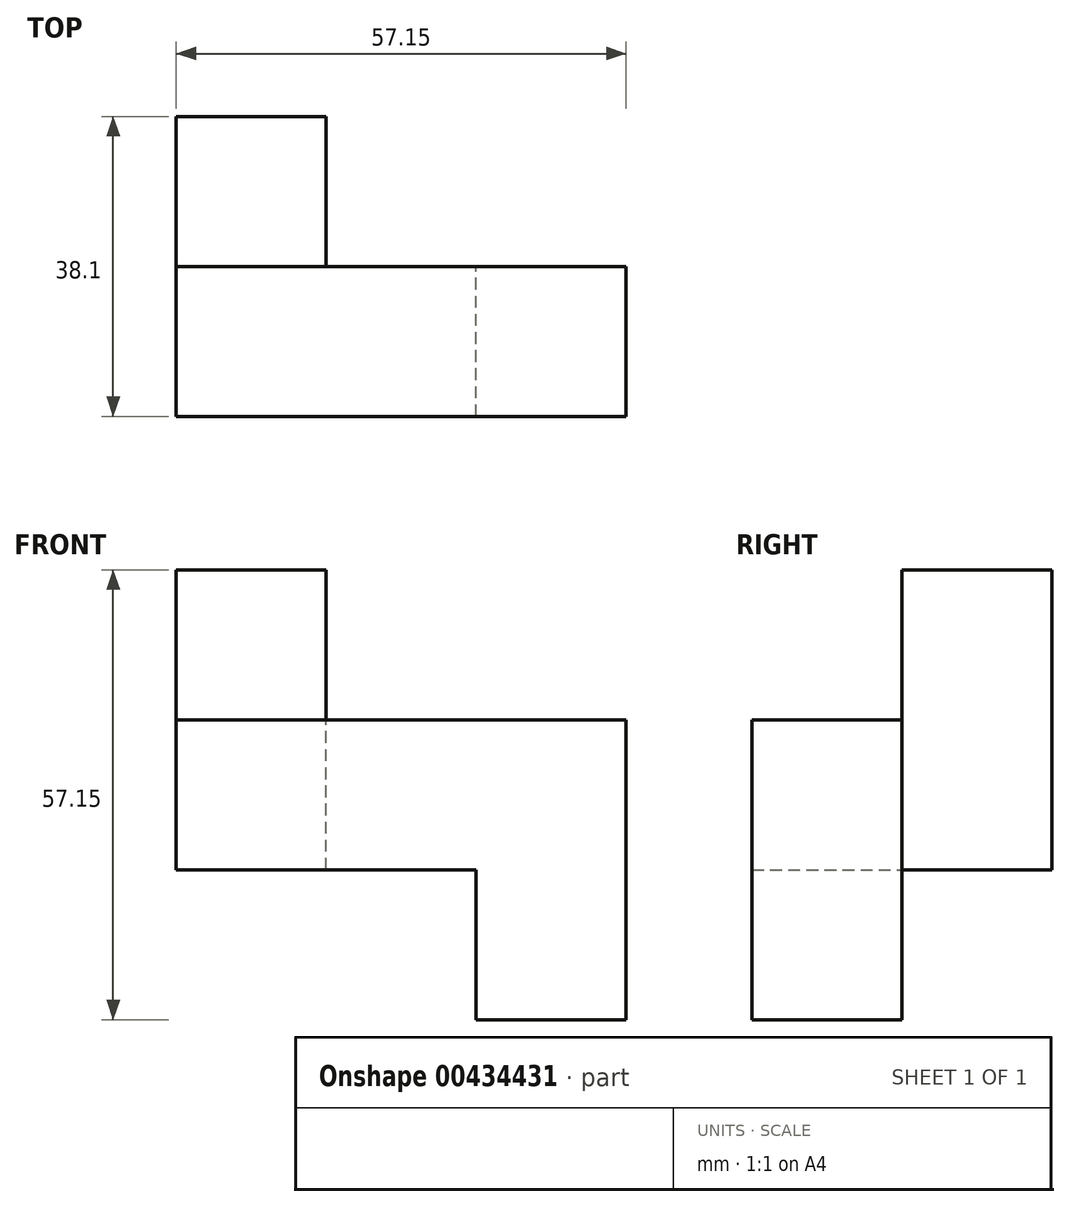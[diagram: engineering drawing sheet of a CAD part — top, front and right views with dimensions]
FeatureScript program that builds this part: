
annotation { "Feature Type Name" : "Feature", "Feature Type Description" : "" }
export const myFeature = defineFeature(function(context is Context, id is Id, definition is map)
    precondition{}
    {
        {
            var Q0;
            Q0=qCreatedBy(makeId("Front.planeOp"),FACE);
            var sketch = newSketch(context, id + "F0", { "sketchPlane" : qUnion([Q0])});
            skLineSegment(sketch, "E0", {"start": v(-62.24, 53.61) * mm, "end": v(-62.24, -50.56) * mm});
            skLineSegment(sketch, "E1", {"start": v(-62.24, -50.56) * mm, "end": v(31.63, -50.56) * mm});
            skLineSegment(sketch, "E2", {"start": v(31.63, -50.56) * mm, "end": v(31.63, 53.61) * mm});
            skLineSegment(sketch, "E3", {"start": v(31.63, 53.61) * mm, "end": v(-62.24, 53.61) * mm});
            skLineSegment(sketch, "E4", {"start": v(-43.91, 19.05) * mm, "end": v(-43.91, -38.1) * mm});
            skLineSegment(sketch, "E5", {"start": v(-43.91, 19.05) * mm, "end": v(-24.86, 19.05) * mm});
            skLineSegment(sketch, "E6", {"start": v(-24.86, 19.05) * mm, "end": v(-24.86, 0) * mm});
            skLineSegment(sketch, "E7", {"start": v(-24.86, 0) * mm, "end": v(13.24, 0) * mm});
            skLineSegment(sketch, "E8", {"start": v(13.24, 0) * mm, "end": v(13.24, -38.1) * mm});
            skLineSegment(sketch, "E9", {"start": v(13.24, -38.1) * mm, "end": v(-43.91, -38.1) * mm});
            skLineSegment(sketch, "E10", {"start": v(-43.91, -38.1) * mm, "end": v(-24.86, -38.1) * mm});
            skPoint(sketch, "E11.endSnap0", {"position": v(13.24, -19.05) * mm});
            skLineSegment(sketch, "E12", {"start": v(-24.86, -19.05) * mm, "end": v(-43.91, -19.05) * mm});
            skLineSegment(sketch, "E13", {"start": v(-43.91, -19.05) * mm, "end": v(-5.81, -19.05) * mm});
            skPoint(sketch, "E13.endSnap0", {"position": v(-5.81, 0) * mm});
            skLineSegment(sketch, "E14", {"start": v(-5.81, -19.05) * mm, "end": v(-5.81, -38.1) * mm});
            skLineSegment(sketch, "E15", {"start": v(-5.81, -19.05) * mm, "end": v(13.24, -19.05) * mm});
            skLineSegment(sketch, "E16", {"start": v(-24.86, 0) * mm, "end": v(-43.91, 0) * mm});
            skLineSegment(sketch, "E17", {"start": v(-24.86, -19.05) * mm, "end": v(-24.86, 0) * mm});
            skSolve(sketch);
        }
        {
            var Q0;
            {var subQ4=sQuery(id+"F0.wireOp",EDGE,"E14");Q0=makeQuery(id+"F0.imprint","IMPRINT",FACE,{"disambiguationData":[TD([[makeQuery(id+"F0.imprint","IMPRINT",EDGE,{"derivedFrom":subQ4}),1.0]])]});}
            extrude(context, id + "F1", {"entities" : qUnion([Q0]), "depth" : 38.1 * mm});
        }
        {
            var Q0;
            {var subQ0=sQuery(id+"F0.wireOp",EDGE,"E7");Q0=makeQuery(id+"F0.imprint","IMPRINT",FACE,{"disambiguationData":[TD([[makeQuery(id+"F0.imprint","IMPRINT",EDGE,{"derivedFrom":subQ0}),-1.0]])]});}
            extrude(context, id + "F2", {"entities" : qUnion([Q0]), "operationType" : NewBodyOperationType.ADD, "depth" : 19.05 * mm});
        }
        {
            var Q0;
            {var subQ3=sQuery(id+"F0.wireOp",EDGE,"E16");Q0=makeQuery(id+"F0.imprint","IMPRINT",FACE,{"disambiguationData":[TD([[makeQuery(id+"F0.imprint","IMPRINT",EDGE,{"derivedFrom":subQ3}),1.0]])]});}
            extrude(context, id + "F3", {"entities" : qUnion([Q0]), "operationType" : NewBodyOperationType.ADD, "depth" : 19.05 * mm});
        }
        {
            var Q0;
            {var subQ3=sQuery(id+"F0.wireOp",EDGE,"E16");Q0=makeQuery(id+"F0.imprint","IMPRINT",FACE,{"disambiguationData":[TD([[makeQuery(id+"F0.imprint","IMPRINT",EDGE,{"derivedFrom":subQ3}),1.0]])]});}
            extrude(context, id + "F4", {"entities" : qUnion([Q0]), "operationType" : NewBodyOperationType.ADD, "oppositeDirection" : true, "depth" : 19.05 * mm});
        }
        {
            var Q0;
            {var subQ0=sQuery(id+"F0.wireOp",EDGE,"E5");Q0=makeQuery(id+"F0.imprint","IMPRINT",FACE,{"disambiguationData":[TD([[makeQuery(id+"F0.imprint","IMPRINT",EDGE,{"derivedFrom":subQ0}),-1.0]])]});}
            extrude(context, id + "F5", {"entities" : qUnion([Q0]), "operationType" : NewBodyOperationType.ADD, "oppositeDirection" : true, "depth" : 19.05 * mm});
        }
        {
            var Q0;
            Q0=makeQuery(id+"F1.opExtrude","SWEPT_FACE",FACE,{"disambiguationData":[OSD([sQuery(id+"F0.wireOp",EDGE,"E14")])]});
            var sketch = newSketch(context, id + "F6", { "sketchPlane" : qUnion([Q0])});
            skLineSegment(sketch, "E18", {"start": v(19.05, -19.05) * mm, "end": v(19.05, -38.1) * mm});
            skSolve(sketch);
        }
        {
            var Q0;
            {var subQ0=sQuery(id+"F6.wireOp",EDGE,"E18");Q0=makeQuery(id+"F6.imprint","IMPRINT",FACE,{"disambiguationData":[TD([[makeQuery(id+"F6.imprint","IMPRINT",EDGE,{"derivedFrom":subQ0}),1.0]])]});}
            extrude(context, id + "F7", {"entities" : qUnion([Q0]), "operationType" : NewBodyOperationType.REMOVE, "oppositeDirection" : true, "depth" : 25.4 * mm});
        }
    });
